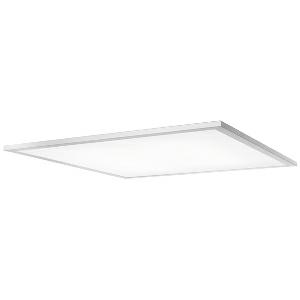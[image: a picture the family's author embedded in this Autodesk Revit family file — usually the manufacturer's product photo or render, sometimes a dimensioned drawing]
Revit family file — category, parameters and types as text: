
# Revit family: dotoo_fit_-_dfe_4000_830_d_sm625_00808116_b20a
name_source: partatom
category: Lighting Fixtures
units: mm (PartAtom-declared; Revit-internal decimal feet)

## family parameters
Cut with Voids When Loaded = No
Host = Face
Light Source = No
Part Type = Normal
Room Calculation Point = No
Round Connector Dimension = Use Diameter
Shared = No

## types (1)
- DOTOO.fit - DFE 4000/830/D SM625 (1 x LED, 3900 lm, 4000K)
    Apparent Load = 30 VA
    Approval mark = CE
    CIE Flux Codes = 66 90 98 100 100
    Color Rendering = 80-89
    Color Temperature = 4000K
    Control Gear = Electronic ballast
    Default Elevation = 1800 mm
    Description = DFE 4000/830/D|Recessed modular luminaire|light source:  |work equipment: Electronic ballast|connected load: 220-240V, 50/60Hz|Power consumption: approx. 30 W|standby: approx. 0,50|power factor: approx. 0,900|luminous flux: 3900 lm|luminous efficacy: 130 lm/W|light distribution: Direct|direct ratio: approx. 100 %|colour temperature: Warm white, ca. 3000 K|color rendering index (CRI): >= 80|chromaticity tolerance:  3 SDCM|System of protection: IP 20|class of protection: II|technology: Continuously dimmable|operation: External|luminaire body|material: Sectional aluminium|colour: White|weight (net): approx. 3.1 kg|mains lead: 0.50 m Connector|glare control: Prism aperture|luminance(L65): <= 2600 cd/m|unified glare rating(4H 8H): <=  19|special features: DALI Load 1x, TouchDIM - dimming via standard switch, Direct light component with edge light and light-guide technology for homogenous light exit, Flicker-free, System dimension 625 x 625 mm, Strain relief with the possibility of through-wiring|
    Height = 0 mm  [stored 0 ft]
    Lamp = 1 x LED
    Lamp Light Flux = 3900 lm
    Lamp count = 1
    Length = 622 mm
    Luminous efficacy = 130 lm/W
    Manufacturer = Waldmann
    ModVariant = No
    Model = 00808116
    Mounting Place = Ceiling
    Mounting Type = Recessed
    Number of Poles = 1
    OnlyDefault = Yes
    Power Factor = 1
    Product Name = DOTOO.fit - DFE 4000/830/D SM625
    Product group = Recessed luminaire
    ProductGroupID = 4
    Protection Class = Protection class II
    Protection Degree = IP 20
    RLX_Detail_Level = 1
    RLX_Emergency_Light_Flux = 0 lm
    RLX_Emergency_Type = 0
    RLX_Emergency_Type_DB = No
    RlxData = <blob elided: 37673 chars, md5=a71bdfe7>
    Socket = socket
    Standby Power = 0 W
    System Light Flux = 3900 lm
    System Power = 30 W
    Type Comments = Product without accessories
    Type Image = 113328000-00692486.jpg
    URL = http://relux.com
    VarID = ---
    Voltage = 230 V
    Voltage Range = 220-240 V
    Weight = 0.00 kg
    Width = 622 mm

note: [stored X ft] marks values corroborated as IEEE doubles in the binary element streams (Revit-internal decimal feet)

## geometry (parser evidence)
native form markers: Blend x4, Sweep x11
no freeform markers — native parametric forms only
